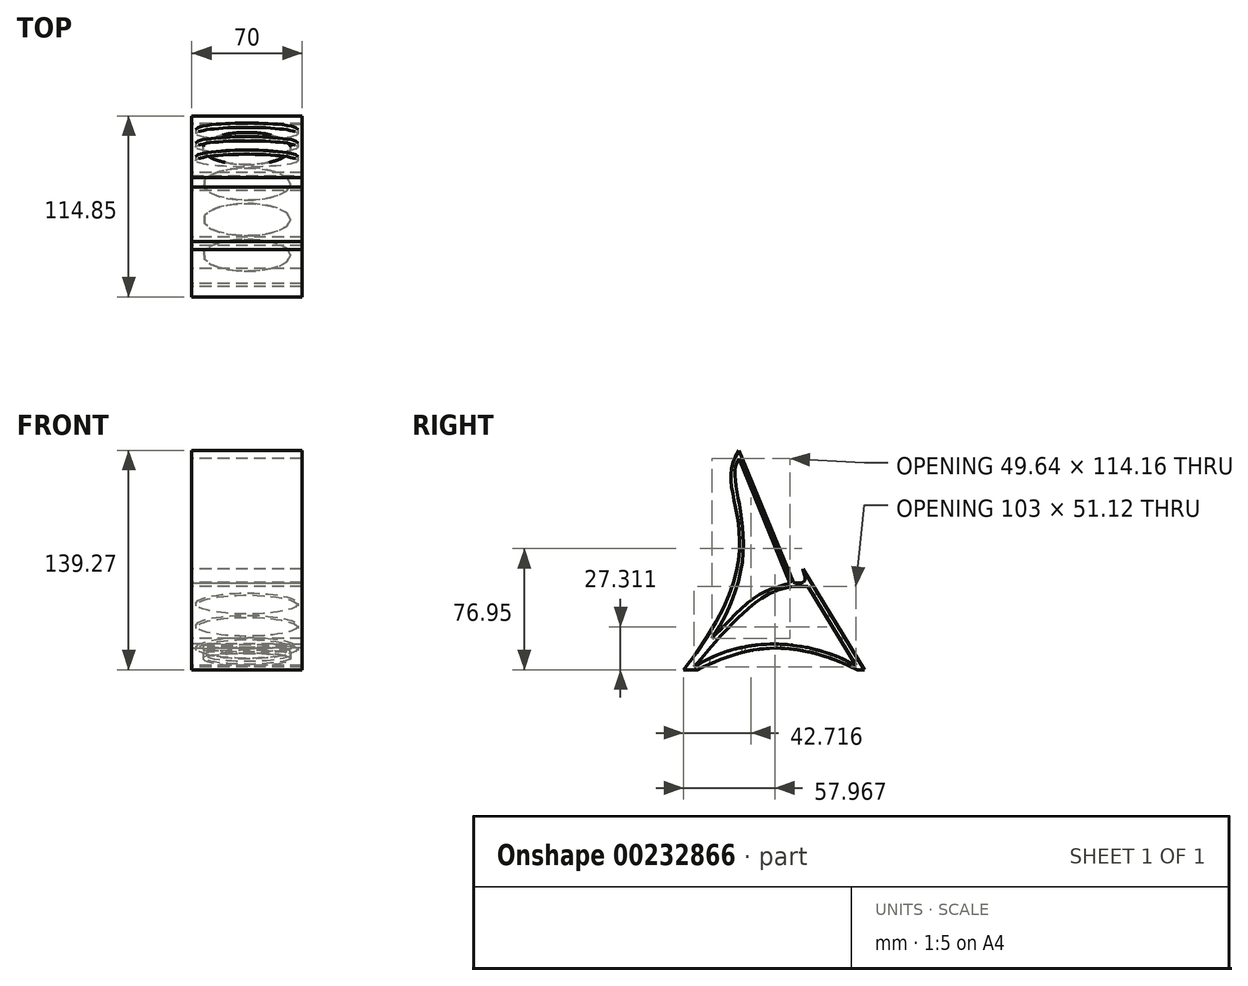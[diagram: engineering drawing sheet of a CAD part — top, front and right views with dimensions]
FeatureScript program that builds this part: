
annotation { "Feature Type Name" : "Feature", "Feature Type Description" : "" }
export const myFeature = defineFeature(function(context is Context, id is Id, definition is map)
    precondition{}
    {
        {
            var Q0;
            Q0=qCreatedBy(makeId("Right.planeOp"),FACE);
            var sketch = newSketch(context, id + "F0", { "sketchPlane" : qUnion([Q0])});
            skFitSpline(sketch, "E0", {"points": [v(-65.05, 0) * mm, v(-29.92, 139.27) * mm], "startDerivative": vector(201.71, 254.1) * mm, "endDerivative": vector(62.07, 87.75) * mm});
            skFitSpline(sketch, "E1", {"points": [v(-56.41, 0) * mm, v(45.2, 0) * mm], "startDerivative": vector(85.43, 39.38) * mm, "endDerivative": vector(140.76, -68.45) * mm});
            skFitSpline(sketch, "E2", {"points": [v(49.8, 0) * mm, v(10.74, 63.83) * mm], "startDerivative": vector(-39.06, 63.83) * mm, "endDerivative": vector(-39.06, 63.83) * mm});
            skLineSegment(sketch, "E3", {"start": v(-29.92, 139.27) * mm, "end": v(4.83, 55.39) * mm});
            skFitSpline(sketch, "E4", {"points": [v(-47.16, 19.87) * mm, v(4.83, 55.39) * mm], "startDerivative": vector(67.93, 68.5) * mm, "endDerivative": vector(79.95, 18.57) * mm});
            skFitSpline(sketch, "E5", {"points": [v(-47.16, 19.87) * mm, v(-29.9, 134.03) * mm], "startDerivative": vector(120.76, 180.8) * mm, "endDerivative": vector(35.66, 50.36) * mm});
            skFitSpline(sketch, "E6", {"points": [v(-58.58, 1.75) * mm, v(13.98, 52.87) * mm], "startDerivative": vector(111.53, 132.38) * mm, "endDerivative": vector(70.15, -3.04) * mm});
            skFitSpline(sketch, "E7", {"points": [v(-58.58, 1.75) * mm, v(44.42, 2.6) * mm], "startDerivative": vector(96.07, 60.59) * mm, "endDerivative": vector(95.42, -52.13) * mm});
            skFitSpline(sketch, "E8", {"points": [v(4.83, 55.39) * mm, v(10.74, 63.83) * mm], "startDerivative": vector(36.77, -7.47) * mm, "endDerivative": vector(2.44, 4) * mm});
            skLineSegment(sketch, "E9", {"start": v(-65.05, 0) * mm, "end": v(-56.41, 0) * mm});
            skLineSegment(sketch, "E10", {"start": v(45.2, 0) * mm, "end": v(49.8, 0) * mm});
            skLineSegment(sketch, "E11", {"start": v(13.98, 52.87) * mm, "end": v(44.42, 2.6) * mm});
            skLineSegment(sketch, "E12", {"start": v(-29.9, 134.03) * mm, "end": v(2.49, 54.83) * mm});
            skSolve(sketch);
        }
        {
            var Q0;
            Q0=makeQuery(id+"F0.imprint","IMPRINT",FACE,{"disambiguationData":[TD([[makeQuery(id+"F0.imprint","IMPRINT",EDGE,{"derivedFrom":sQuery(id+"F0.wireOp",EDGE,"E0")}),-1.0]])]});
            extrude(context, id + "F1", {"entities" : qUnion([Q0]), "depth" : 70 * mm});
        }
        {
            var Q0;
            Q0=makeQuery(id+"F1.opExtrude","SWEPT_FACE",FACE,{"disambiguationData":[OSD([sQuery(id+"F0.wireOp",EDGE,"3ry2OGPV-gmds-sl4L-2rMf-ZdiDfTWU18HU")])]});
            var Q1;
            Q1=makeQuery(id+"F1.opExtrude","SWEPT_EDGE",EDGE,{"disambiguationData":[OSD([sQuery(id+"F0.wireOp",EDGE,"E0"),sQuery(id+"F0.wireOp",EDGE,"E3")])]});
            cPlane(context, id + "F2", {"entities" : qUnion([Q0, Q1]), "cplaneType" : CPlaneType.LINE_ANGLE, "offset" : 25 * mm, "angle" : 90 * degree, "width" : 150 * mm, "height" : 150 * mm});
        }
        {
            var Q0;
            Q0=qCreatedBy(id+"F2.planeOp",FACE);
            var sketch = newSketch(context, id + "F3", { "sketchPlane" : qUnion([Q0])});
            skLineSegment(sketch, "E13.bottom", {"start": v(0, -20) * mm, "end": v(70, -20) * mm});
            skLineSegment(sketch, "E13.top", {"start": v(0, 53.36) * mm, "end": v(70, 53.36) * mm});
            skLineSegment(sketch, "E13.left", {"start": v(0, -20) * mm, "end": v(0, 53.36) * mm});
            skLineSegment(sketch, "E13.right", {"start": v(70, -20) * mm, "end": v(70, 53.36) * mm});
            skSolve(sketch);
        }
        {
            var Q0;
            Q0=qCreatedBy(id+"F2.planeOp",FACE);
            var sketch = newSketch(context, id + "F4", { "sketchPlane" : qUnion([Q0])});
            skEllipse(sketch, "E14", {"center": v(35, -10.4) * mm, "majorRadius": 32.5 * mm, "minorRadius": 8.5 * mm, "majorAxis": v(-1, 0)});
            skEllipse(sketch, "E15.0.1.0", {"center": v(35, 7.6) * mm, "majorRadius": 32.5 * mm, "minorRadius": 8.5 * mm, "majorAxis": v(-1, 0)});
            skEllipse(sketch, "E15.0.2.0", {"center": v(35, 25.6) * mm, "majorRadius": 32.5 * mm, "minorRadius": 8.5 * mm, "majorAxis": v(-1, 0)});
            skEllipse(sketch, "E15.0.3.0", {"center": v(35, 43.6) * mm, "majorRadius": 32.5 * mm, "minorRadius": 8.5 * mm, "majorAxis": v(-1, 0)});
            skLineSegment(sketch, "E15.direction1", {"start": v(35, -10.4) * mm, "end": v(60, -10.4) * mm, "construction": true});
            skLineSegment(sketch, "E15.direction2", {"start": v(35, -10.4) * mm, "end": v(35, 7.6) * mm, "construction": true});
            skSolve(sketch);
        }
        {
            var Q0;
            Q0 = qSketchRegion(id + "F4", true);
            extrude(context, id + "F5", {"entities" : qUnion([Q0]), "operationType" : NewBodyOperationType.REMOVE, "endBound" : BoundingType.THROUGH_ALL, "depth" : 25 * mm});
        }
        {
            var Q0;
            Q0=qCreatedBy(id+"F2.planeOp",FACE);
            var sketch = newSketch(context, id + "F6", { "sketchPlane" : qUnion([Q0])});
            skEllipse(sketch, "E16", {"center": v(35.28, -29.36) * mm, "majorRadius": 17.78 * mm, "minorRadius": 3.94 * mm, "majorAxis": v(-1, 0)});
            skSolve(sketch);
        }
        {
            var Q0;
            Q0 = qSketchRegion(id + "F6", true);
            extrude(context, id + "F7", {"entities" : qUnion([Q0]), "operationType" : NewBodyOperationType.REMOVE, "endBound" : BoundingType.THROUGH_ALL, "depth" : 25 * mm});
        }
        {
            var Q0;
            Q0=makeQuery(id+"F1.opExtrude","SWEPT_FACE",FACE,{"disambiguationData":[OSD([sQuery(id+"F0.wireOp",EDGE,"E11")])]});
            var sketch = newSketch(context, id + "F8", { "sketchPlane" : qUnion([Q0])});
            skEllipse(sketch, "E17", {"center": v(35, 23.43) * mm, "majorRadius": 32.5 * mm, "minorRadius": 7.82 * mm, "majorAxis": v(1, 0)});
            skEllipse(sketch, "E18.0.1.0", {"center": v(35, 6.93) * mm, "majorRadius": 32.5 * mm, "minorRadius": 7.82 * mm, "majorAxis": v(1, 0)});
            skEllipse(sketch, "E18.0.2.0", {"center": v(35, -9.57) * mm, "majorRadius": 32.5 * mm, "minorRadius": 7.82 * mm, "majorAxis": v(1, 0)});
            skLineSegment(sketch, "E18.direction1", {"start": v(35, 23.43) * mm, "end": v(57.03, 23.43) * mm, "construction": true});
            skLineSegment(sketch, "E18.direction2", {"start": v(35, 23.43) * mm, "end": v(35, 6.93) * mm, "construction": true});
            skSolve(sketch);
        }
        {
            var Q0;
            Q0 = qSketchRegion(id + "F8", true);
            var Q1;
            Q1=makeQuery(id+"F1.opExtrude","SWEPT_FACE",FACE,{"disambiguationData":[OSD([sQuery(id+"F0.wireOp",EDGE,"E2")])]});
            extrude(context, id + "F9", {"entities" : qUnion([Q0]), "operationType" : NewBodyOperationType.REMOVE, "endBound" : BoundingType.UP_TO_SURFACE, "oppositeDirection" : true, "endBoundEntityFace" : qUnion([Q1]), "depth" : 25 * mm});
        }
        {
            var Q0;
            Q0=qCreatedBy(makeId("Top.planeOp"),FACE);
            var sketch = newSketch(context, id + "F10", { "sketchPlane" : qUnion([Q0])});
            skEllipse(sketch, "E19", {"center": v(35, -38.54) * mm, "majorRadius": 27.85 * mm, "minorRadius": 10.2 * mm, "majorAxis": v(1, 0)});
            skEllipse(sketch, "E20.0.1.0", {"center": v(35, -15.94) * mm, "majorRadius": 27.85 * mm, "minorRadius": 10.2 * mm, "majorAxis": v(1, 0)});
            skEllipse(sketch, "E20.0.2.0", {"center": v(35, 6.66) * mm, "majorRadius": 27.85 * mm, "minorRadius": 10.2 * mm, "majorAxis": v(1, 0)});
            skEllipse(sketch, "E20.0.3.0", {"center": v(35, 29.26) * mm, "majorRadius": 27.85 * mm, "minorRadius": 10.2 * mm, "majorAxis": v(1, 0)});
            skLineSegment(sketch, "E20.direction1", {"start": v(35, -38.54) * mm, "end": v(60, -38.54) * mm, "construction": true});
            skLineSegment(sketch, "E20.direction2", {"start": v(35, -38.54) * mm, "end": v(35, -15.94) * mm, "construction": true});
            skSolve(sketch);
        }
        {
            var Q0;
            Q0 = qSketchRegion(id + "F10", true);
            var Q1;
            Q1=makeQuery(id+"F1.opExtrude","SWEPT_FACE",FACE,{"disambiguationData":[OSD([sQuery(id+"F0.wireOp",EDGE,"E7")])]});
            extrude(context, id + "F11", {"entities" : qUnion([Q0]), "operationType" : NewBodyOperationType.REMOVE, "endBound" : BoundingType.UP_TO_SURFACE, "endBoundEntityFace" : qUnion([Q1]), "depth" : 25 * mm});
        }
    });
